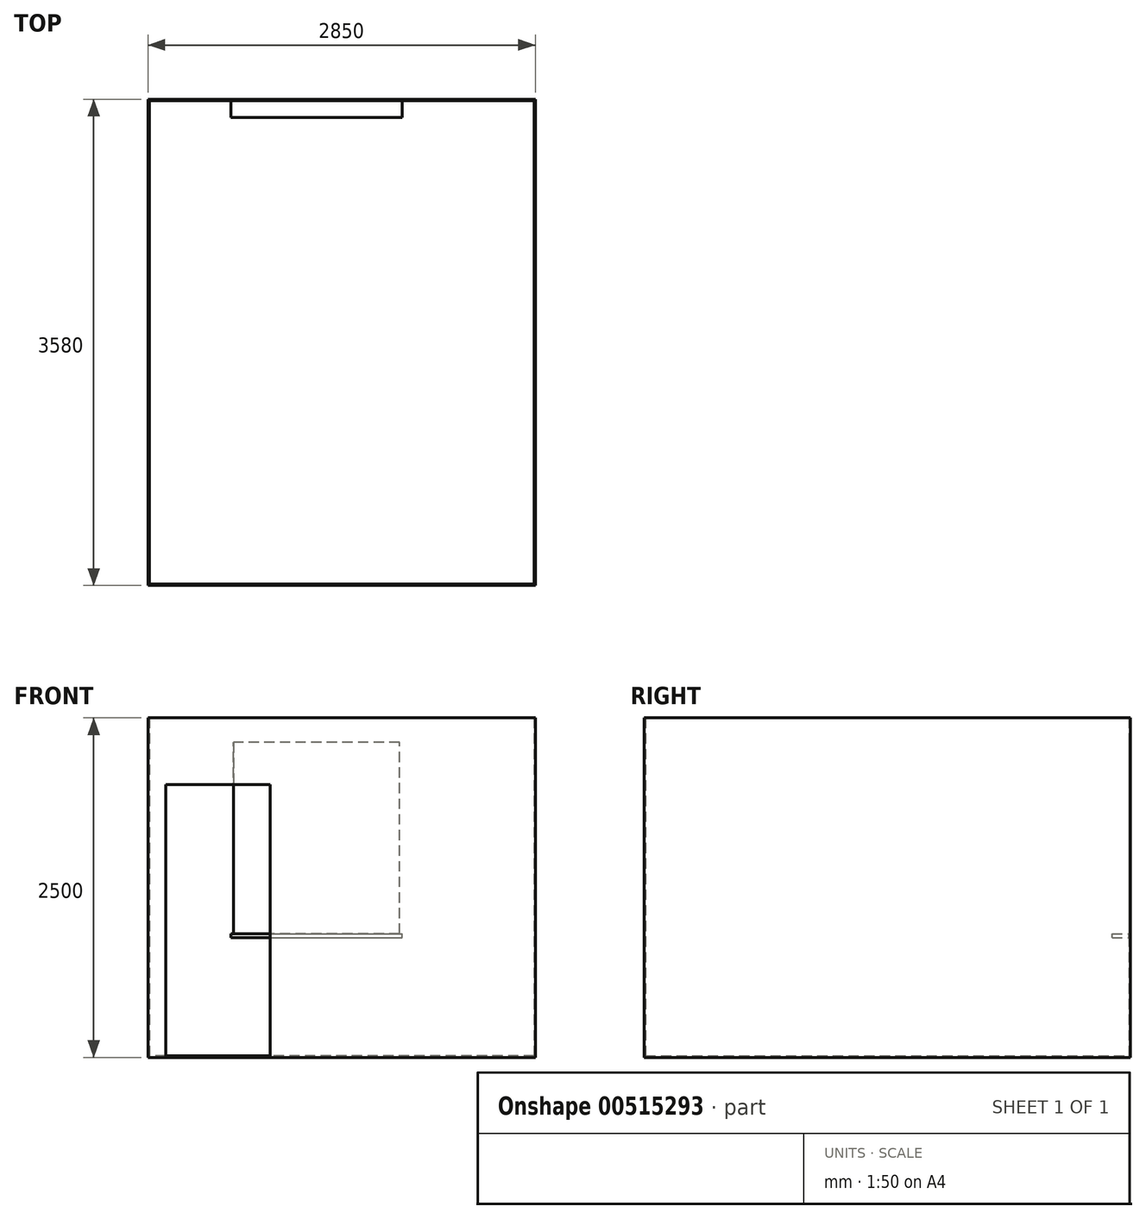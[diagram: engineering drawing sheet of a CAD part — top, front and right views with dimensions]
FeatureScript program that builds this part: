
annotation { "Feature Type Name" : "Feature", "Feature Type Description" : "" }
export const myFeature = defineFeature(function(context is Context, id is Id, definition is map)
    precondition{}
    {
        {
            var Q0;
            Q0=qCreatedBy(makeId("Top.planeOp"),FACE);
            var sketch = newSketch(context, id + "F0", { "sketchPlane" : qUnion([Q0])});
            skLineSegment(sketch, "E0.bottom", {"start": v(1425, 1790) * mm, "end": v(-1425, 1790) * mm});
            skLineSegment(sketch, "E0.top", {"start": v(1425, -1790) * mm, "end": v(-1425, -1790) * mm});
            skLineSegment(sketch, "E0.left", {"start": v(1425, 1790) * mm, "end": v(1425, -1790) * mm});
            skLineSegment(sketch, "E0.right", {"start": v(-1425, 1790) * mm, "end": v(-1425, -1790) * mm});
            skPoint(sketch, "E0.middle", {"position": v(0, 0) * mm});
            skSolve(sketch);
        }
        {
            var Q0;
            Q0 = qSketchRegion(id + "F0", true);
            extrude(context, id + "F1", {"entities" : qUnion([Q0]), "depth" : 10 * mm, "offsetDistance" : 25 * mm});
        }
        {
            var Q0;
            Q0=makeQuery(id+"F0.imprint","IMPRINT",FACE,{"disambiguationData":[TD([[makeQuery(id+"F0.imprint","IMPRINT",EDGE,{"derivedFrom":sQuery(id+"F0.wireOp",EDGE,"E0.bottom")}),1.0]])]});
            var sketch = newSketch(context, id + "F2", { "sketchPlane" : qUnion([Q0])});
            skLineSegment(sketch, "E1.bottom", {"start": v(-1415, 1780) * mm, "end": v(1415, 1780) * mm});
            skLineSegment(sketch, "E1.top", {"start": v(-1415, -1780) * mm, "end": v(1415, -1780) * mm});
            skLineSegment(sketch, "E1.left", {"start": v(-1415, 1780) * mm, "end": v(-1415, -1780) * mm});
            skLineSegment(sketch, "E1.right", {"start": v(1415, 1780) * mm, "end": v(1415, -1780) * mm});
            skPoint(sketch, "E1.middle", {"position": v(0, 0) * mm});
            skLineSegment(sketch, "E2.bottom", {"start": v(-1425, 1790) * mm, "end": v(1425, 1790) * mm});
            skLineSegment(sketch, "E2.top", {"start": v(-1425, -1790) * mm, "end": v(1425, -1790) * mm});
            skLineSegment(sketch, "E2.left", {"start": v(-1425, 1790) * mm, "end": v(-1425, -1790) * mm});
            skLineSegment(sketch, "E2.right", {"start": v(1425, 1790) * mm, "end": v(1425, -1790) * mm});
            skSolve(sketch);
        }
        {
            var Q0;
            Q0 = qSketchRegion(id + "F2", true);
            extrude(context, id + "F3", {"entities" : qUnion([Q0]), "operationType" : NewBodyOperationType.ADD, "depth" : 2500 * mm, "offsetDistance" : 25 * mm});
        }
        {
            var Q0;
            Q0=makeQuery(id+"F3.opExtrude","SWEPT_FACE",FACE,{"disambiguationData":[OSD([sQuery(id+"F2.wireOp",EDGE,"E2.top")])]});
            var sketch = newSketch(context, id + "F4", { "sketchPlane" : qUnion([Q0])});
            skLineSegment(sketch, "E3.bottom", {"start": v(-1295, 10) * mm, "end": v(-525, 10) * mm});
            skLineSegment(sketch, "E3.top", {"start": v(-1295, 2010) * mm, "end": v(-525, 2010) * mm});
            skLineSegment(sketch, "E3.left", {"start": v(-1295, 10) * mm, "end": v(-1295, 2010) * mm});
            skLineSegment(sketch, "E3.right", {"start": v(-525, 10) * mm, "end": v(-525, 2010) * mm});
            skSolve(sketch);
        }
        {
            var Q0;
            Q0 = qSketchRegion(id + "F4", true);
            extrude(context, id + "F5", {"entities" : qUnion([Q0]), "operationType" : NewBodyOperationType.REMOVE, "endBound" : BoundingType.UP_TO_NEXT, "oppositeDirection" : true, "depth" : 25 * mm, "offsetDistance" : 25 * mm});
        }
        {
            var Q0;
            Q0=makeQuery(id+"F3.opExtrude","SWEPT_FACE",FACE,{"disambiguationData":[OSD([sQuery(id+"F2.wireOp",EDGE,"E2.bottom")])]});
            var sketch = newSketch(context, id + "F6", { "sketchPlane" : qUnion([Q0])});
            skLineSegment(sketch, "E4.bottom", {"start": v(-425, 910) * mm, "end": v(795, 910) * mm});
            skLineSegment(sketch, "E4.top", {"start": v(-425, 2320) * mm, "end": v(795, 2320) * mm});
            skLineSegment(sketch, "E4.left", {"start": v(-425, 910) * mm, "end": v(-425, 2320) * mm});
            skLineSegment(sketch, "E4.right", {"start": v(795, 910) * mm, "end": v(795, 2320) * mm});
            skSolve(sketch);
        }
        {
            var Q0;
            Q0 = qSketchRegion(id + "F6", true);
            extrude(context, id + "F7", {"entities" : qUnion([Q0]), "operationType" : NewBodyOperationType.REMOVE, "endBound" : BoundingType.UP_TO_NEXT, "oppositeDirection" : true, "depth" : 25 * mm, "offsetDistance" : 25 * mm});
        }
        {
            var Q0;
            Q0=makeQuery(id+"F3.opExtrude","SWEPT_FACE",FACE,{"disambiguationData":[OSD([sQuery(id+"F2.wireOp",EDGE,"E1.bottom")])]});
            var sketch = newSketch(context, id + "F8", { "sketchPlane" : qUnion([Q0])});
            skLineSegment(sketch, "E5.bottom", {"start": v(-815, 880) * mm, "end": v(445, 880) * mm});
            skLineSegment(sketch, "E5.top", {"start": v(-815, 910) * mm, "end": v(445, 910) * mm});
            skLineSegment(sketch, "E5.left", {"start": v(-815, 880) * mm, "end": v(-815, 910) * mm});
            skLineSegment(sketch, "E5.right", {"start": v(445, 880) * mm, "end": v(445, 910) * mm});
            skSolve(sketch);
        }
        {
            var Q0;
            Q0 = qSketchRegion(id + "F8", true);
            extrude(context, id + "F9", {"entities" : qUnion([Q0]), "depth" : 125 * mm, "offsetDistance" : 25 * mm});
        }
    });
